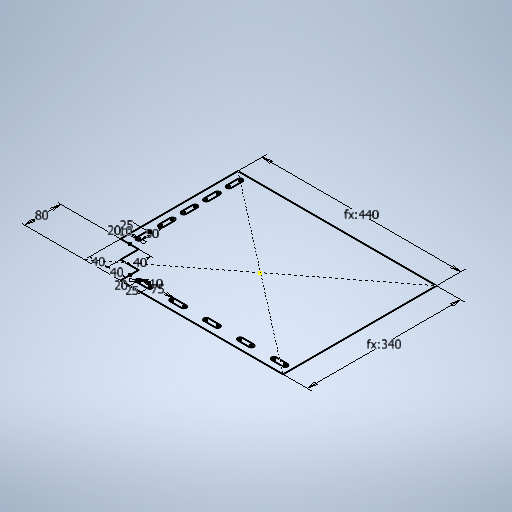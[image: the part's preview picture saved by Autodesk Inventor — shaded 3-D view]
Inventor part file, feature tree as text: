
AUTODESK INVENTOR PART (.ipt)
format: ipt  version: 2025 (Build 290162000, 162)  size: 269,312 bytes
history: native  units: mm
features: sketch x3
ambient origin geometry x8: Origin, YZ Plane, XZ Plane, XY Plane, X Axis, Y Axis, Z Axis, Center Point
feature tree (3):
  sketch  "Sketch1"  dims[d14=440.0mm]
  sketch  "Sketch Rectangular Pattern3"  dims[d15=340.0mm]
  sketch  "Sketch Rectangular Pattern4"  dims[d16=40.0mm d17=80.0mm d18=40.0mm d19=40.0mm d40=10.0mm d41=25.0mm d42=20.0mm d43=50.0mm d45=50.0mm d46=10.0mm d48=10.0mm d50=10.0mm d51=20.0mm d52=25.0mm d53=50.0mm d55=75.0mm d56=10.0mm d58=10.0mm]
